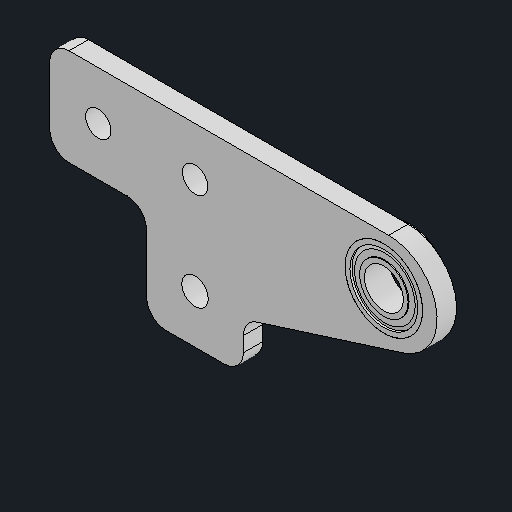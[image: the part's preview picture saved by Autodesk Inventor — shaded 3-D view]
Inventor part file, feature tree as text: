
AUTODESK INVENTOR PART (.ipt)
format: ipt  version: 2024.2 (Build 282272000, 272)  size: 134,656 bytes
history: native  units: mm
features: other x3, fillet x1
ambient origin geometry x8: Origin, YZ Plane, XZ Plane, XY Plane, X Axis, Y Axis, Z Axis, Center Point
bodies: Body1 (feature_tree), Body2 (feature_tree)
feature tree (4):
  other  "솔리드1"
  other  "솔리드2"
  fillet  "Fillet1"  [1 undecoded]
  other  "Cut-Revolve1"
note: 1 required parameter value undecoded (feature->parameter linkage not recoverable at this tier; creation-order binding heuristic only, values carry confidence <= 0.55)
